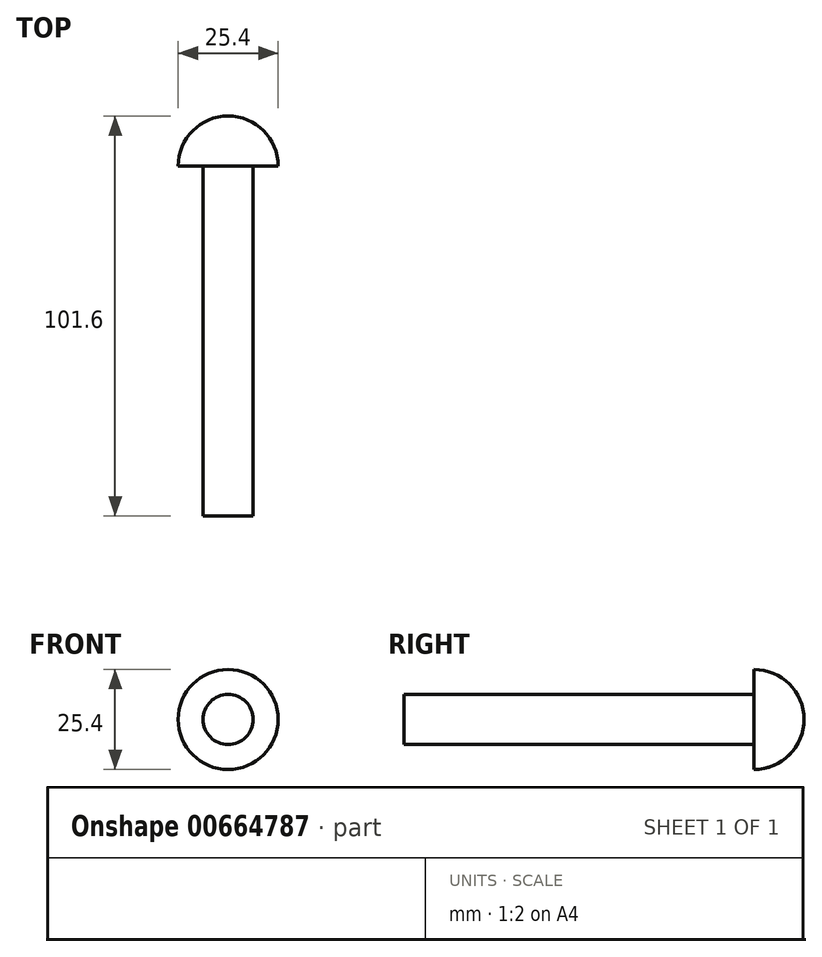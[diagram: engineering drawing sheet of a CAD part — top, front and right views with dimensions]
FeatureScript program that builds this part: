
annotation { "Feature Type Name" : "Feature", "Feature Type Description" : "" }
export const myFeature = defineFeature(function(context is Context, id is Id, definition is map)
    precondition{}
    {
        {
            var Q0;
            Q0=qCreatedBy(makeId("Front.planeOp"),FACE);
            var sketch = newSketch(context, id + "F0", { "sketchPlane" : qUnion([Q0])});
            skCircle(sketch, "E0", {"center": v(0, 0) * mm, "radius": 6.35 * mm});
            skSolve(sketch);
        }
        {
            var Q0;
            Q0 = qSketchRegion(id + "F0", true);
            extrude(context, id + "F1", {"entities" : qUnion([Q0]), "depth" : 101.6 * mm, "offsetDistance" : 25.4 * mm});
        }
        {
            var Q0;
            Q0=qCreatedBy(makeId("Front.planeOp"),FACE);
            var sketch = newSketch(context, id + "F2", { "sketchPlane" : qUnion([Q0])});
            skCircle(sketch, "E1", {"center": v(0, 0) * mm, "radius": 12.7 * mm});
            skSolve(sketch);
        }
        {
            var Q0;
            Q0 = qSketchRegion(id + "F2", true);
            extrude(context, id + "F3", {"entities" : qUnion([Q0]), "operationType" : NewBodyOperationType.ADD, "depth" : 12.7 * mm, "offsetDistance" : 25.4 * mm});
        }
        {
            var Q0;
            Q0=makeQuery(id+"F3.opExtrude","CAP_EDGE",EDGE,{"disambiguationData":[OSD([sQuery(id+"F2.wireOp",EDGE,"E1")])],"isStart":true});
            fillet(context, id + "F4", {"entities" : qUnion([Q0]), "radius" : 12.7 * mm, "tangentPropagation" : true, "allowEdgeOverflow" : false});
        }
    });
